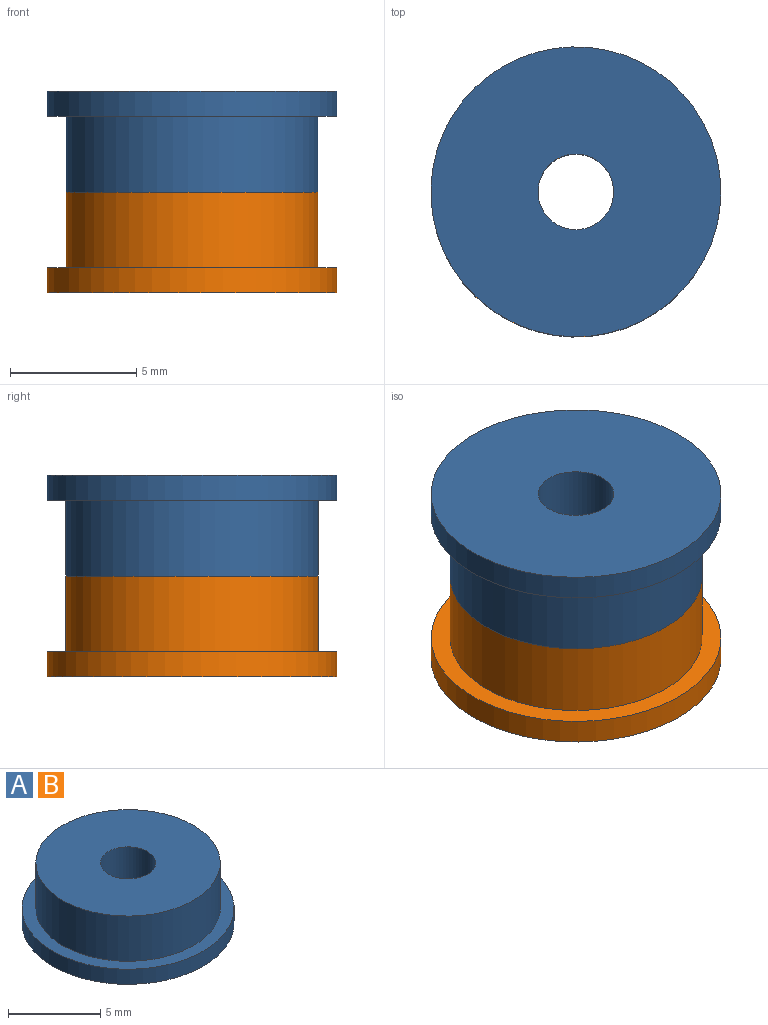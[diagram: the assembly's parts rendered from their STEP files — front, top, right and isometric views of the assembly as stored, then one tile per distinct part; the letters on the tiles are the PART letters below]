
ASSEMBLY  parts=2 mates=1
PART A: 6 faces, bbox 11.5x11.5x4 mm
  f0: cylinder r=5.75mm len=11.5mm, axis (0,0,-1), area 36.1mm2, adj f1,f2
  f1: plane 11.5x11.5mm, normal (0,0,1), area 25.3mm2, adj f0,f3
  f2: plane 11.5x11.5mm, normal (0,0,-1), area 96.8mm2, adj f0,f4
  f3: cylinder r=5mm len=10mm, axis (0,0,-1), area 94.2mm2, adj f1,f5
  f4: cylinder r=1.5mm len=4mm, axis (0,0,-1), area 37.7mm2, adj f2,f5
  f5: plane 10x10mm, normal (0,0,1), area 71.5mm2, adj f3,f4
PART B: same geometry as A
PLACE A rot(axis=(1,0,0),180deg) t=(-12.2,-3.94,10.66)mm
PLACE B t=(-12.2,-3.94,2.66)mm
MATE fastened A.f0 <-> B.f0  axis (0,0,1) through (-12.2,-3.94,6.66)mm
